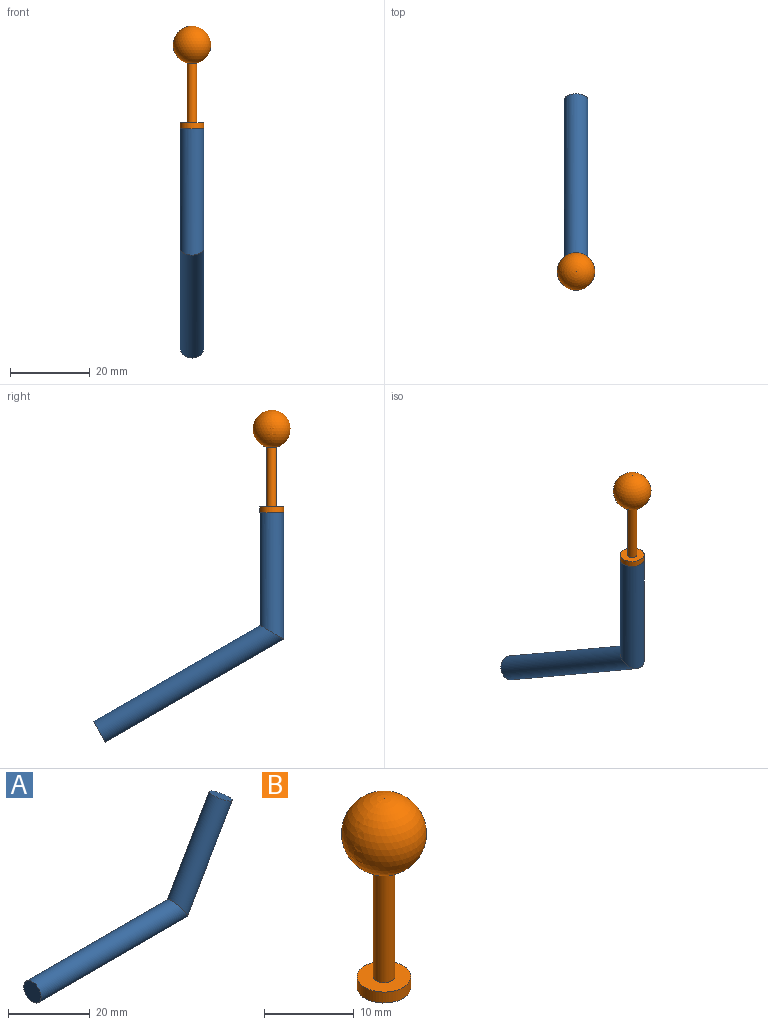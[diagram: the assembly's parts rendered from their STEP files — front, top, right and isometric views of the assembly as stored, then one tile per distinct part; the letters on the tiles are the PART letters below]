
ASSEMBLY  parts=2 mates=1
PART A: 4 faces, bbox 67.6x6x30.5 mm
  f0: plane 6x5.2mm, normal (0.5,0,0.87), area 28.3mm2, adj f2
  f1: plane 6x6mm, normal (-1,0,0), area 28.3mm2, adj f3
  f2: cylinder r=3mm len=30.48mm, axis (0.5,0,0.87), area 565.5mm2, adj f0,f3
  f3: cylinder r=3mm len=51.73mm, axis (1,0,0), area 942.5mm2, adj f1,f2
PART B: 5 faces, bbox 9.5x9.5x25.8 mm
  f0: plane 6x6mm, normal (0,0,-1), area 28.3mm2, adj f1
  f1: cylinder r=3mm len=6mm, axis (0,0,-1), area 28.3mm2, adj f0,f2
  f2: plane 6x6mm, normal (0,0,1), area 23.7mm2, adj f1,f3
  f3: cylinder r=1.2mm len=15mm, axis (0,0,-1), area 113.4mm2, adj f2,f4
  f4: sphere r=4.75mm, area 278.9mm2, adj f3
PLACE A rot(axis=(-0.25,-0.25,-0.94),93.8deg) t=(48.97,82.66,-57.42)mm
PLACE B t=(48.97,39.36,-2.42)mm
MATE slider A.f2 <-> B.f1  axis (0,0,1) through (48.97,39.36,-2.42)mm
